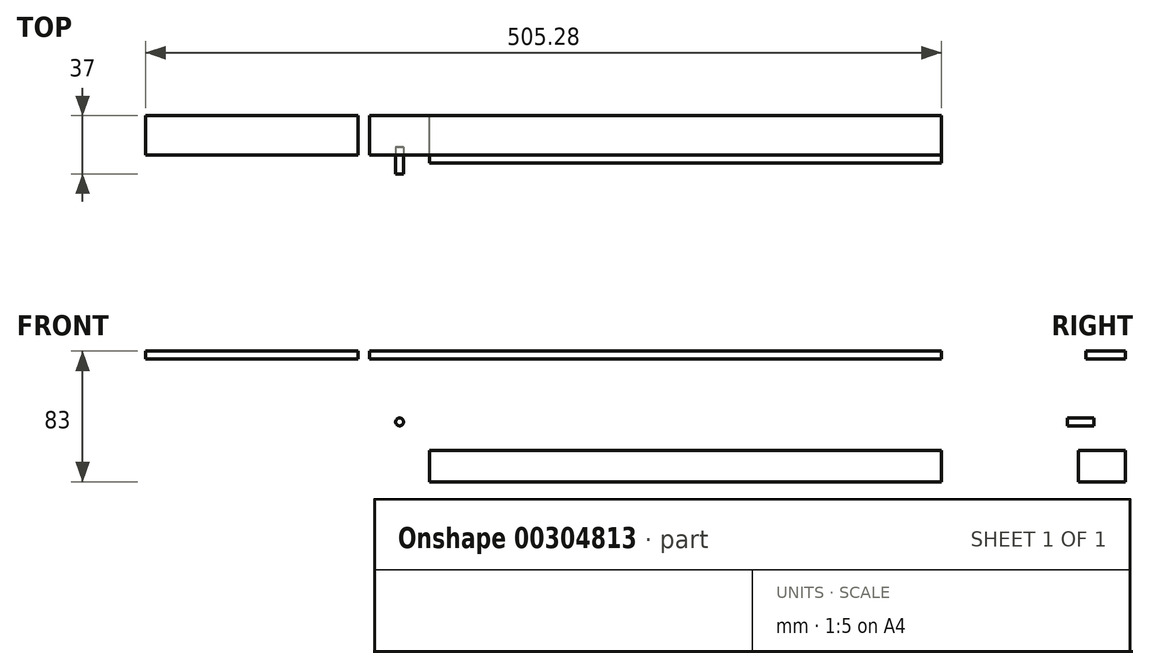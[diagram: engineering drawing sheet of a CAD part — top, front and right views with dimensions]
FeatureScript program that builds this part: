
annotation { "Feature Type Name" : "Feature", "Feature Type Description" : "" }
export const myFeature = defineFeature(function(context is Context, id is Id, definition is map)
    precondition{}
    {
        {
            var Q0;
            Q0=qCreatedBy(makeId("Front.planeOp"),FACE);
            var sketch = newSketch(context, id + "F0", { "sketchPlane" : qUnion([Q0])});
            skLineSegment(sketch, "E0.bottom", {"start": v(0, 0) * mm, "end": v(363, 0) * mm});
            skLineSegment(sketch, "E0.top", {"start": v(0, 5) * mm, "end": v(363, 5) * mm});
            skLineSegment(sketch, "E0.left", {"start": v(0, 0) * mm, "end": v(0, 5) * mm});
            skLineSegment(sketch, "E0.right", {"start": v(363, 0) * mm, "end": v(363, 5) * mm});
            skLineSegment(sketch, "E1.bottom", {"start": v(-7.28, 0) * mm, "end": v(-142.28, 0) * mm});
            skLineSegment(sketch, "E1.top", {"start": v(-7.28, 5) * mm, "end": v(-142.28, 5) * mm});
            skLineSegment(sketch, "E1.left", {"start": v(-7.28, 0) * mm, "end": v(-7.28, 5) * mm});
            skLineSegment(sketch, "E1.right", {"start": v(-142.28, 0) * mm, "end": v(-142.28, 5) * mm});
            skPoint(sketch, "E2", {"position": v(-74.78, 0) * mm});
            skLineSegment(sketch, "E3.bottom", {"start": v(363, -78) * mm, "end": v(18, -78) * mm});
            skLineSegment(sketch, "E3.top", {"start": v(363, -58) * mm, "end": v(18, -58) * mm});
            skLineSegment(sketch, "E3.left", {"start": v(363, -78) * mm, "end": v(363, -58) * mm});
            skLineSegment(sketch, "E3.right", {"start": v(18, -78) * mm, "end": v(18, -58) * mm});
            skLineSegment(sketch, "E4.bottom", {"start": v(18, -58) * mm, "end": v(38, -58) * mm});
            skLineSegment(sketch, "E4.top", {"start": v(18, -78) * mm, "end": v(38, -78) * mm});
            skLineSegment(sketch, "E4.left", {"start": v(18, -58) * mm, "end": v(18, -78) * mm});
            skLineSegment(sketch, "E4.right", {"start": v(38, -58) * mm, "end": v(38, -78) * mm});
            skPoint(sketch, "E5", {"position": v(28, -58) * mm});
            skLineSegment(sketch, "E6.bottom", {"start": v(60, -5) * mm, "end": v(0, -5) * mm});
            skLineSegment(sketch, "E6.top", {"start": v(60, -63) * mm, "end": v(0, -63) * mm});
            skLineSegment(sketch, "E6.left", {"start": v(60, -5) * mm, "end": v(60, -63) * mm});
            skLineSegment(sketch, "E6.right", {"start": v(0, -5) * mm, "end": v(0, -63) * mm});
            skCircle(sketch, "E7", {"center": v(5, -10) * mm, "radius": 1.4 * mm});
            skPoint(sketch, "E8", {"position": v(0, 0) * mm});
            skCircle(sketch, "E9", {"center": v(5, -35) * mm, "radius": 1.4 * mm});
            skCircle(sketch, "E10", {"center": v(53, -35) * mm, "radius": 1.4 * mm});
            skLineSegment(sketch, "E11.top", {"start": v(8.45, -29) * mm, "end": v(49.45, -29) * mm});
            skPoint(sketch, "E12", {"position": v(19, -40) * mm});
            skCircle(sketch, "E13.MirrorC", {"center": v(53, -45) * mm, "radius": 1.4 * mm});
            skCircle(sketch, "E14.MirrorC", {"center": v(5, -45) * mm, "radius": 1.4 * mm});
            skLineSegment(sketch, "E15.MirrorCS", {"start": v(8.45, -51) * mm, "end": v(49.45, -51) * mm});
            skCircle(sketch, "E16", {"center": v(19, -40) * mm, "radius": 12.5 * mm});
            skLineSegment(sketch, "E17", {"start": v(49.45, -29) * mm, "end": v(49.45, -51) * mm});
            skLineSegment(sketch, "E18", {"start": v(8.45, -29) * mm, "end": v(8.45, -51) * mm});
            skPoint(sketch, "E19", {"position": v(8.45, -40) * mm});
            skPoint(sketch, "E20", {"position": v(-117, 0) * mm});
            skLineSegment(sketch, "E21.bottom", {"start": v(5, -58) * mm, "end": v(15, -58) * mm});
            skLineSegment(sketch, "E21.top", {"start": v(5, -53) * mm, "end": v(15, -53) * mm});
            skLineSegment(sketch, "E21.left", {"start": v(5, -58) * mm, "end": v(5, -53) * mm});
            skLineSegment(sketch, "E21.right", {"start": v(15, -58) * mm, "end": v(15, -53) * mm});
            skLineSegment(sketch, "E22.bottom", {"start": v(45, -58) * mm, "end": v(55, -58) * mm});
            skLineSegment(sketch, "E22.top", {"start": v(45, -53) * mm, "end": v(55, -53) * mm});
            skLineSegment(sketch, "E22.left", {"start": v(45, -58) * mm, "end": v(45, -53) * mm});
            skLineSegment(sketch, "E22.right", {"start": v(55, -58) * mm, "end": v(55, -53) * mm});
            skSolve(sketch);
        }
        {
            var Q0;
            {var subQ9=sQuery(id+"F0.wireOp",EDGE,"E4.bottom");Q0=makeQuery(id+"F0.imprint","IMPRINT",FACE,{"disambiguationData":[TD([[makeQuery(id+"F0.imprint","IMPRINT",EDGE,{"derivedFrom":subQ9}),1.0]])]});}
            var Q1;
            Q1=makeQuery(id+"F0.imprint","IMPRINT",FACE,{"disambiguationData":[TD([[makeQuery(id+"F0.imprint","IMPRINT",EDGE,{"derivedFrom":sQuery(id+"F0.wireOp",EDGE,"E4.bottom")}),-1.0]])]});
            var Q2;
            {var subQ0=sQuery(id+"F0.wireOp",EDGE,"E4.right");Q2=makeQuery(id+"F0.imprint","IMPRINT",FACE,{"disambiguationData":[TD([[makeQuery(id+"F0.imprint","IMPRINT",EDGE,{"derivedFrom":subQ0}),1.0]])]});}
            extrude(context, id + "F1", {"entities" : qUnion([Q0, Q1, Q2]), "depth" : 5 * mm});
        }
        {
            var Q0;
            Q0=makeQuery(id+"F0.imprint","IMPRINT",FACE,{"disambiguationData":[TD([[makeQuery(id+"F0.imprint","IMPRINT",EDGE,{"derivedFrom":sQuery(id+"F0.wireOp",EDGE,"E1.bottom")}),-1.0]])]});
            var Q1;
            Q1=makeQuery(id+"F0.imprint","IMPRINT",FACE,{"disambiguationData":[TD([[makeQuery(id+"F0.imprint","IMPRINT",EDGE,{"derivedFrom":sQuery(id+"F0.wireOp",EDGE,"E0.bottom")}),1.0]])]});
            var Q2;
            {var subQ0=sQuery(id+"F0.wireOp",EDGE,"E3.left");Q2=makeQuery(id+"F0.imprint","IMPRINT",FACE,{"disambiguationData":[TD([[makeQuery(id+"F0.imprint","IMPRINT",EDGE,{"derivedFrom":subQ0}),1.0]])]});}
            var Q3;
            {var subQ0=sQuery(id+"F0.wireOp",EDGE,"E4.right");Q3=makeQuery(id+"F0.imprint","IMPRINT",FACE,{"disambiguationData":[TD([[makeQuery(id+"F0.imprint","IMPRINT",EDGE,{"derivedFrom":subQ0}),1.0]])]});}
            var Q4;
            Q4=makeQuery(id+"F0.imprint","IMPRINT",FACE,{"disambiguationData":[TD([[makeQuery(id+"F0.imprint","IMPRINT",EDGE,{"derivedFrom":sQuery(id+"F0.wireOp",EDGE,"E4.bottom")}),-1.0]])]});
            extrude(context, id + "F2", {"entities" : qUnion([Q0, Q1, Q2, Q3, Q4]), "operationType" : NewBodyOperationType.ADD, "oppositeDirection" : true, "depth" : 25 * mm});
        }
        {
            var Q0;
            Q0=qCreatedBy(makeId("Front.planeOp"),FACE);
            cPlane(context, id + "F3", {"entities" : qUnion([Q0]), "cplaneType" : CPlaneType.OFFSET, "offset" : (17 - 5) * mm, "width" : 150 * mm, "height" : 150 * mm});
        }
        {
            var Q0;
            Q0=qCreatedBy(id+"F3.planeOp",FACE);
            var sketch = newSketch(context, id + "F4", { "sketchPlane" : qUnion([Q0])});
            skCircle(sketch, "E23", {"center": v(19, -40) * mm, "radius": 2.5 * mm});
            skSolve(sketch);
        }
        {
            var Q0;
            Q0=makeQuery(id+"F4.imprint","IMPRINT",FACE,{"disambiguationData":[TD([[makeQuery(id+"F4.imprint","IMPRINT",EDGE,{"derivedFrom":sQuery(id+"F4.wireOp",EDGE,"E23")}),1.0]])]});
            extrude(context, id + "F5", {"entities" : qUnion([Q0]), "oppositeDirection" : true, "depth" : 17 * mm});
        }
    });
